# Revit family: 20.1 Верхняя торцевая панель с гибкой вставкой ANR P2
name_source: partatom
category: Оборудование
revit_build: Autodesk Revit 2016 (Build: 20161004_0715(x64)
units: mm (PartAtom-declared; Revit-internal decimal feet)

## family parameters
Всегда вертикально = Да
На основе рабочей плоскости = Нет
Общий = Нет
При загрузке вырезать с полостями = Нет
Размер круглого соединителя = Использовать диаметр
Тип детали = Нормальный
Точка расчета площади = Нет

## types (8) — shared parameters
Д = 150 мм
Д1 = 130 мм
Единица измерения = шт.
Завод изготовитель = KORF
Ключевая пометка = Вентиляция
Материал = Сталь серая
Наименование и тех.хар-ка = Верхняя торцевая панель с мягкой вставкой
Раздел = ОВ
гибкая вставка = резина

## per-type parameters (varying)
| type | А | А1 | А2 | А3 | Б | Б1 | Б2 | Б3 | Высота | Р | Середина | Ширина |
| ANR 6 P2 | 1040 мм | 1010 мм | 1100 мм | 1080 мм | 540 мм | 510 мм | 1100 мм | 1080 мм | 489 мм | 26 мм | 270 мм | 989 мм |
| ANR 7 P2 | 1040 мм | 1010 мм | 1100 мм | 1080 мм | 540 мм | 510 мм | 1320 мм | 1300 мм | 489 мм | 26 мм | 270 мм | 989 мм |
| ANR 8 P2 | 1240 мм | 1210 мм | 1320 мм | 1300 мм | 540 мм | 510 мм | 1320 мм | 1300 мм | 479 мм | 31 мм | 270 мм | 1179 мм |
| ANR 12 P2 | 1358 мм | 1328 мм | 1435 мм | 1415 мм | 1040 мм | 1010 мм | 1435 мм | 1415 мм | 973 мм | 34 мм | 520 мм | 1291 мм |
| ANR 20 P2 | 1582 мм | 1552 мм | 1660 мм | 1640 мм | 1040 мм | 1010 мм | 1660 мм | 1640 мм | 962 мм | 39 мм | 520 мм | 1504 мм |
| ANR 25 P2 | 1968 мм | 1938 мм | 2045 мм | 2025 мм | 1040 мм | 1010 мм | 2045 мм | 2025 мм | 943 мм | 49 мм | 520 мм | 1871 мм |
| ANR 30 P2 | 2408 мм | 2381 мм | 2485 мм | 2465 мм | 1040 мм | 1010 мм | 2045 мм | 2025 мм | 921 мм | 59 мм | 520 мм | 2289 мм |
| ANR 35 P2 | 2408 мм | 2381 мм | 2485 мм | 2465 мм | 1540 мм | 1512 мм | 2485 мм | 2465 мм | 1421 мм | 59 мм | 770 мм | 2289 мм |

note: column(s) folded — value = type name in every type: Тип, марка, обозначение
